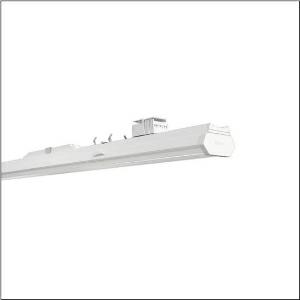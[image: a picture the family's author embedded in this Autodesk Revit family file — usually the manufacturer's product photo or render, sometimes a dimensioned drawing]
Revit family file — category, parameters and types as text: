
# Revit family: licross_r__11_protected_mo_51td12dn495g_4259
name_source: partatom
category: Lighting Fixtures
units: mm (PartAtom-declared; Revit-internal decimal feet)

## family parameters
Cut with Voids When Loaded = No
Host = Face
Light Source = No
Part Type = Normal
Room Calculation Point = No
Round Connector Dimension = Use Diameter
Shared = No

## types (1)
- --- (1 x LED, 9980 lm, 57.1 W, 4000K)
    Apparent Load = 57 VA
    CIE Flux Codes = 73 92 98 99 100
    Color Rendering = 80
    Color Temperature = 4000K
    Default Elevation = 1800 mm
    Description = Licross® 11 Protected MO, luminaire insert, of sheet steel, galvanised, coil coated, white, length: 1.500mm, width: 90mm, height: 101mm, LED rated luminous flux: 9.980lm, light colour: 840, control gear: DALI 2, with plug, 5-pole, with phase selection, mains connection: 220..240V, AC, 50/60Hz, rated input power: 57W, halogen-free wiring, primary optical cover: cover, of PMMA, light emission: direct distribution, primary light characteristic: symmetric, protection rating (complete): IP54, insulation class (complete): insulation class I (protective earthing), certification: CE, ENEC, VDE, UKCA, protection symbol: D if used in an environment with non-conductive dust loads with corresponding accessories, impact resistance: IK06, permissible ambient temperature for indoor applications: -25..+35°C, corresponds to IFS (International Featured Standards) requirements for safety and quality in the food industry, reducing of maximum allowable ambient temperature of 5°C with ceiling mounting, LABS conformity tested according to VDMA 24364:2018-05, packaging unit: 1 piece
    Height = 92 mm
    Lamp = 1 x LED
    Lamp Light Flux = 9980 lm
    Lamp Power = 57.1 W
    Lamp count = 1
    Length = 1500 mm
    Luminous efficacy = 175 lm/W
    Manufacturer = Siteco
    ModVariant = No
    Model = 51TD12DN495G
    Mounting Place = Ceiling
    Mounting Type = Pendant
    Number of Poles = 1
    OnlyDefault = Yes
    Power Factor = 1
    Product Name = Licross® 11 Protected MO
    Product group = luminaire insert
    ProductGroupID = 902
    Protection Class = Protection class I
    Protection Degree = IP 54
    RLX_Detail_Level = 1
    RLX_Emergency_Light_Flux = 0 lm
    RLX_Emergency_Type = 0
    RLX_Emergency_Type_DB = No
    RlxData = <blob elided: 24457 chars, md5=ccdbc2bb>
    Socket = socket
    Standby Power = 0 W
    System Light Flux = 9980 lm
    System Power = 57 W
    Type Comments = factory setting: luminous flux: 100 % | dim-lin: 254 | 378 mA
    Type Image = l_1256145.jpg
    URL = http://relux.com
    VarID = @adj_101182
    Voltage = 0 V
    Weight = 0.00 kg
    Width = 88 mm

## geometry (parser evidence)
native form markers: Blend x4, Sweep x12
no freeform markers — native parametric forms only
